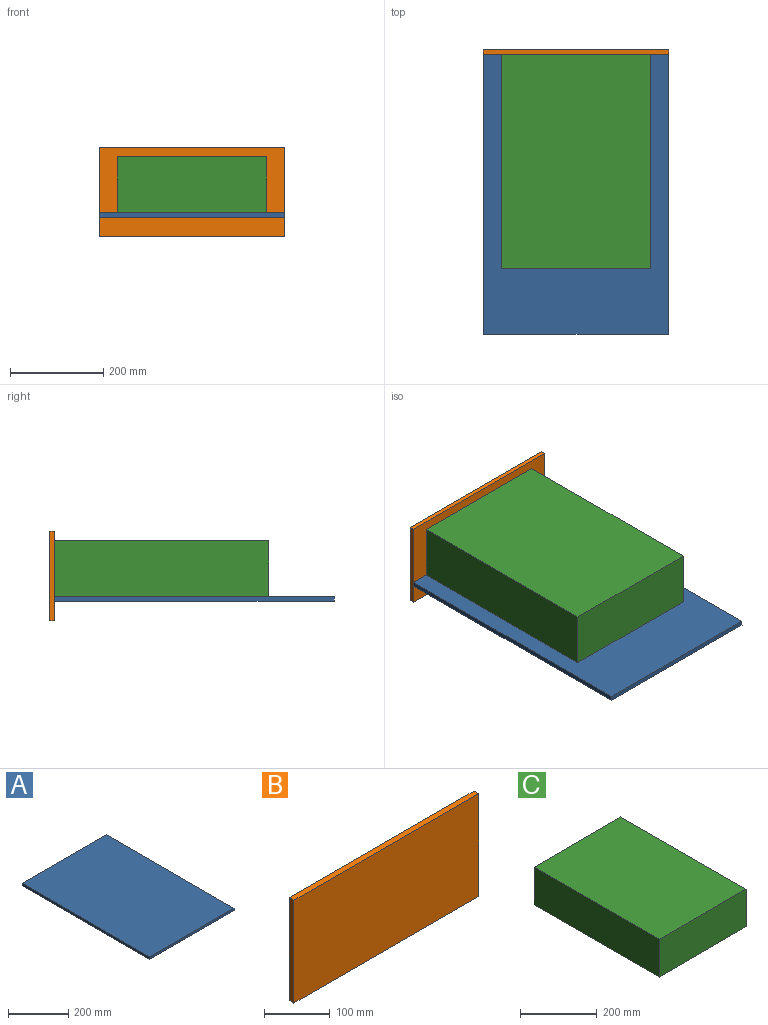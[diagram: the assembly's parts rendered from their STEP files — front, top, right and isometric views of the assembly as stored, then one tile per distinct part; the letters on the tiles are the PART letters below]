
ASSEMBLY  parts=3 mates=3
PART A: 6 faces, bbox 396x600x10 mm
  f0: plane 600x396mm, normal (0,0,1), area 237600mm2, adj f1,f3,f4,f5
  f1: plane 600x10mm, normal (-1,0,0), area 6000mm2, adj f0,f2,f4,f5
  f2: plane 600x396mm, normal (0,0,-1), area 237600mm2, adj f1,f3,f4,f5
  f3: plane 600x10mm, normal (1,0,0), area 6000mm2, adj f0,f2,f4,f5
  f4: plane 396x10mm, normal (0,1,0), area 3960mm2, adj f0,f1,f2,f3
  f5: plane 396x10mm, normal (0,-1,0), area 3960mm2, adj f0,f1,f2,f3
PART B: 6 faces, bbox 398x10x191.7 mm
  f0: plane 398x10mm, normal (0,0,1), area 3980mm2, adj f1,f3,f4,f5
  f1: plane 191.68x10mm, normal (-1,0,0), area 1916.8mm2, adj f0,f2,f4,f5
  f2: plane 398x10mm, normal (0,0,-1), area 3980mm2, adj f1,f3,f4,f5
  f3: plane 191.68x10mm, normal (1,0,0), area 1916.8mm2, adj f0,f2,f4,f5
  f4: plane 398x191.68mm, normal (0,1,0), area 76287.4mm2, adj f0,f1,f2,f3
  f5: plane 398x191.68mm, normal (0,-1,0), area 76287.4mm2, adj f0,f1,f2,f3
PART C: 6 faces, bbox 320x460x120 mm
  f0: plane 460x320mm, normal (0,0,1), area 147200mm2, adj f1,f3,f4,f5
  f1: plane 460x120mm, normal (-1,0,0), area 55200mm2, adj f0,f2,f4,f5
  f2: plane 460x320mm, normal (0,0,-1), area 147200mm2, adj f1,f3,f4,f5
  f3: plane 460x120mm, normal (1,0,0), area 55200mm2, adj f0,f2,f4,f5
  f4: plane 320x120mm, normal (0,1,0), area 38400mm2, adj f0,f1,f2,f3
  f5: plane 320x120mm, normal (0,-1,0), area 38400mm2, adj f0,f1,f2,f3
PLACE A rot(axis=(0.27,-0.55,-0.79),0deg) t=(-25.53,-385.36,-163.13)mm
PLACE B rot(axis=(0,1,0),180deg) t=(-51.42,214.64,-110.03)mm
PLACE C rot(axis=(0.27,-0.55,-0.79),0deg) t=(136.43,-245.36,-134.88)mm
MATE parallel B.f2 <-> A.f2  axis (0,0,1) through (-52.09,214.64,-21.26)mm
MATE fastened C.f2 <-> A.f0  axis (0,0,-1) through (-52.09,214.64,-161.26)mm
MATE planar A.f4 <-> B.f5  axis (0,1,0) through (-52.09,214.64,-166.26)mm
